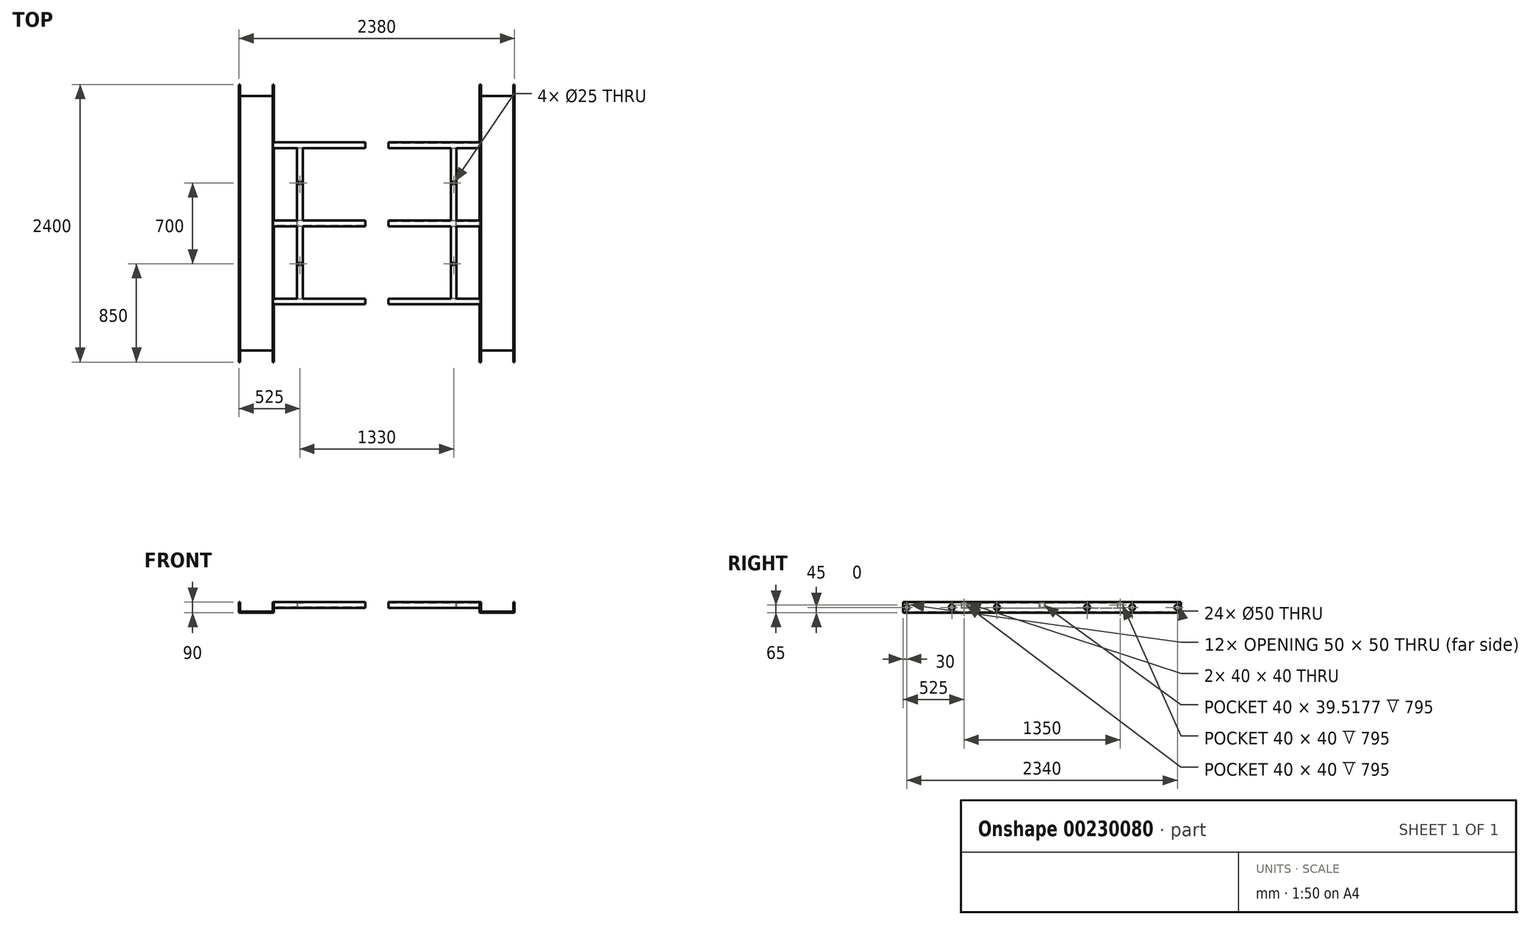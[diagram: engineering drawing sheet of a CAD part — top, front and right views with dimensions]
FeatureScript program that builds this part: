
annotation { "Feature Type Name" : "Feature", "Feature Type Description" : "" }
export const myFeature = defineFeature(function(context is Context, id is Id, definition is map)
    precondition{}
    {
        {
            var Q0;
            Q0=qCreatedBy(makeId("Front.planeOp"),FACE);
            var sketch = newSketch(context, id + "F0", { "sketchPlane" : qUnion([Q0])});
            skLineSegment(sketch, "E0", {"start": v(-890, 0) * mm, "end": v(-1190, 0) * mm});
            skLineSegment(sketch, "E1", {"start": v(-1190, 0) * mm, "end": v(-1190, 90) * mm});
            skLineSegment(sketch, "E2", {"start": v(-1190, 90) * mm, "end": v(-1180, 90) * mm});
            skLineSegment(sketch, "E3", {"start": v(-1180, 90) * mm, "end": v(-1180, 10) * mm});
            skLineSegment(sketch, "E4", {"start": v(-1180, 10) * mm, "end": v(-900, 10) * mm});
            skLineSegment(sketch, "E5", {"start": v(-900, 10) * mm, "end": v(-900, 90) * mm});
            skLineSegment(sketch, "E6", {"start": v(-900, 90) * mm, "end": v(-890, 90) * mm});
            skLineSegment(sketch, "E7", {"start": v(-890, 90) * mm, "end": v(-890, 0) * mm});
            skSolve(sketch);
        }
        {
            var Q0;
            Q0 = qSketchRegion(id + "F0", true);
            extrude(context, id + "F1", {"entities" : qUnion([Q0]), "endBound" : BoundingType.SYMMETRIC, "depth" : 2400 * mm});
        }
        {
            var Q0;
            Q0=makeQuery(id+"F1.opExtrude","SWEPT_FACE",FACE,{"disambiguationData":[OSD([sQuery(id+"F0.wireOp",EDGE,"E4")])]});
            var sketch = newSketch(context, id + "F2", { "sketchPlane" : qUnion([Q0])});
            skLineSegment(sketch, "E8.bottom", {"start": v(-1180, 1200) * mm, "end": v(-900, 1200) * mm});
            skLineSegment(sketch, "E8.top", {"start": v(-1180, 1100) * mm, "end": v(-900, 1100) * mm});
            skLineSegment(sketch, "E8.left", {"start": v(-1180, 1200) * mm, "end": v(-1180, 1100) * mm});
            skLineSegment(sketch, "E8.right", {"start": v(-900, 1200) * mm, "end": v(-900, 1100) * mm});
            skLineSegment(sketch, "E9.bottom", {"start": v(-1180, -1200) * mm, "end": v(-900, -1200) * mm});
            skLineSegment(sketch, "E9.top", {"start": v(-1180, -1100) * mm, "end": v(-900, -1100) * mm});
            skLineSegment(sketch, "E9.left", {"start": v(-1180, -1200) * mm, "end": v(-1180, -1100) * mm});
            skLineSegment(sketch, "E9.right", {"start": v(-900, -1200) * mm, "end": v(-900, -1100) * mm});
            skSolve(sketch);
        }
        {
            var Q0;
            Q0 = qSketchRegion(id + "F2", true);
            extrude(context, id + "F3", {"entities" : qUnion([Q0]), "operationType" : NewBodyOperationType.REMOVE, "oppositeDirection" : true, "depth" : 25 * mm});
        }
        {
            var Q0;
            Q0=makeQuery(id+"F1.opExtrude","SWEPT_FACE",FACE,{"disambiguationData":[OSD([sQuery(id+"F0.wireOp",EDGE,"E7")])]});
            var sketch = newSketch(context, id + "F4", { "sketchPlane" : qUnion([Q0])});
            skLineSegment(sketch, "E10.bottom", {"start": v(-700, 90) * mm, "end": v(-650, 90) * mm});
            skLineSegment(sketch, "E10.top", {"start": v(-700, 40) * mm, "end": v(-650, 40) * mm});
            skLineSegment(sketch, "E10.left", {"start": v(-700, 90) * mm, "end": v(-700, 40) * mm});
            skLineSegment(sketch, "E10.right", {"start": v(-650, 90) * mm, "end": v(-650, 40) * mm});
            skLineSegment(sketch, "E11.bottom", {"start": v(650, 90) * mm, "end": v(700, 90) * mm});
            skLineSegment(sketch, "E11.top", {"start": v(650, 40) * mm, "end": v(700, 40) * mm});
            skLineSegment(sketch, "E11.left", {"start": v(650, 90) * mm, "end": v(650, 40) * mm});
            skLineSegment(sketch, "E11.right", {"start": v(700, 90) * mm, "end": v(700, 40) * mm});
            skLineSegment(sketch, "E12.bottom", {"start": v(-25, 90) * mm, "end": v(25, 90) * mm});
            skLineSegment(sketch, "E12.top", {"start": v(-25, 40.48) * mm, "end": v(25, 40.48) * mm});
            skLineSegment(sketch, "E12.left", {"start": v(-25, 90) * mm, "end": v(-25, 40.48) * mm});
            skLineSegment(sketch, "E12.right", {"start": v(25, 90) * mm, "end": v(25, 40.48) * mm});
            skSolve(sketch);
        }
        {
            var Q0;
            Q0 = qSketchRegion(id + "F4", true);
            extrude(context, id + "F5", {"entities" : qUnion([Q0]), "operationType" : NewBodyOperationType.ADD, "depth" : 790 * mm});
        }
        {
            var Q0;
            Q0=makeQuery(id+"F5.opExtrude","SWEPT_FACE",FACE,{"disambiguationData":[OSD([sQuery(id+"F4.wireOp",EDGE,"E11.left")])]});
            var sketch = newSketch(context, id + "F6", { "sketchPlane" : qUnion([Q0])});
            skLineSegment(sketch, "E13.bottom", {"start": v(-690, 90) * mm, "end": v(-640, 90) * mm});
            skLineSegment(sketch, "E13.top", {"start": v(-690, 40) * mm, "end": v(-685, 40) * mm});
            skLineSegment(sketch, "E13.left", {"start": v(-690, 90) * mm, "end": v(-690, 40) * mm});
            skLineSegment(sketch, "E13.right", {"start": v(-640, 90) * mm, "end": v(-640, 85) * mm});
            skLineSegment(sketch, "E14", {"start": v(-640, 85) * mm, "end": v(-685, 85) * mm});
            skLineSegment(sketch, "E15", {"start": v(-685, 85) * mm, "end": v(-685, 40) * mm});
            skSolve(sketch);
        }
        {
            var Q0;
            Q0 = qSketchRegion(id + "F6", true);
            var Q1;
            Q1=makeQuery(id+"F5.opExtrude","SWEPT_FACE",FACE,{"disambiguationData":[OSD([sQuery(id+"F4.wireOp",EDGE,"E10.right")])]});
            extrude(context, id + "F7", {"entities" : qUnion([Q0]), "operationType" : NewBodyOperationType.ADD, "endBound" : BoundingType.UP_TO_SURFACE, "endBoundEntityFace" : qUnion([Q1]), "depth" : 25 * mm});
        }
        {
            var Q0;
            Q0=makeQuery(id+"F5.opExtrude","CAP_FACE",FACE,{"disambiguationData":[OSD([sQuery(id+"F4.wireOp",EDGE,"E10.bottom"),sQuery(id+"F4.wireOp",EDGE,"E10.top"),sQuery(id+"F4.wireOp",EDGE,"E10.left"),sQuery(id+"F4.wireOp",EDGE,"E10.right")])],"isStart":false});
            var Q1;
            Q1=makeQuery(id+"F5.opExtrude","CAP_FACE",FACE,{"disambiguationData":[OSD([sQuery(id+"F4.wireOp",EDGE,"E12.bottom"),sQuery(id+"F4.wireOp",EDGE,"E12.top"),sQuery(id+"F4.wireOp",EDGE,"E12.left"),sQuery(id+"F4.wireOp",EDGE,"E12.right")])],"isStart":false});
            var Q2;
            Q2=makeQuery(id+"F5.opExtrude","CAP_FACE",FACE,{"disambiguationData":[OSD([sQuery(id+"F4.wireOp",EDGE,"E11.bottom"),sQuery(id+"F4.wireOp",EDGE,"E11.top"),sQuery(id+"F4.wireOp",EDGE,"E11.left"),sQuery(id+"F4.wireOp",EDGE,"E11.right")])],"isStart":false});
            shell(context, id + "F8", {"entities" : qUnion([Q0, Q1, Q2]), "thickness" : 5 * mm});
        }
        {
            var Q0;
            Q0=makeQuery(id+"F7.boolean.opBoolean","MERGE",FACE,{"derivedFrom":[makeQuery(id+"F5.boolean.opBoolean","MERGE",FACE,{"derivedFrom":[makeQuery(id+"F1.opExtrude","SWEPT_FACE",FACE,{"disambiguationData":[OSD([sQuery(id+"F0.wireOp",EDGE,"E6")])]}),makeQuery(id+"F5.opExtrude","SWEPT_FACE",FACE,{"disambiguationData":[OSD([sQuery(id+"F4.wireOp",EDGE,"E10.bottom")])]}),makeQuery(id+"F5.opExtrude","SWEPT_FACE",FACE,{"disambiguationData":[OSD([sQuery(id+"F4.wireOp",EDGE,"E11.bottom")])]})]}),makeQuery(id+"F7.opExtrude","SWEPT_FACE",FACE,{"disambiguationData":[OSD([sQuery(id+"F6.wireOp",EDGE,"E13.bottom")])]})]});
            var sketch = newSketch(context, id + "F9", { "sketchPlane" : qUnion([Q0])});
            skCircle(sketch, "E16", {"center": v(-665, 350) * mm, "radius": 12.5 * mm});
            skCircle(sketch, "E17", {"center": v(-665, -350) * mm, "radius": 12.5 * mm});
            skSolve(sketch);
        }
        {
            var Q0;
            Q0 = qSketchRegion(id + "F9", true);
            extrude(context, id + "F10", {"entities" : qUnion([Q0]), "operationType" : NewBodyOperationType.REMOVE, "oppositeDirection" : true, "depth" : 25 * mm});
        }
        {
            var Q0;
            Q0=makeQuery(id+"F1.opExtrude","SWEPT_FACE",FACE,{"disambiguationData":[OSD([sQuery(id+"F0.wireOp",EDGE,"E1")])]});
            var sketch = newSketch(context, id + "F11", { "sketchPlane" : qUnion([Q0])});
            skCircle(sketch, "E18", {"center": v(-1170, 45) * mm, "radius": 25 * mm});
            skPoint(sketch, "E18.centerSnap0", {"position": v(-1200, 45) * mm});
            skCircle(sketch, "E19", {"center": v(-780, 45) * mm, "radius": 25 * mm});
            skCircle(sketch, "E20", {"center": v(780, 45) * mm, "radius": 25 * mm});
            skCircle(sketch, "E21", {"center": v(1170, 45) * mm, "radius": 25 * mm});
            skCircle(sketch, "E22", {"center": v(-390, 45) * mm, "radius": 25 * mm});
            skCircle(sketch, "E23", {"center": v(390, 45) * mm, "radius": 25 * mm});
            skSolve(sketch);
        }
        {
            var Q0;
            Q0 = qSketchRegion(id + "F11", true);
            var Q1;
            Q1=makeQuery(id+"F1.opExtrude","SWEPT_FACE",FACE,{"disambiguationData":[OSD([sQuery(id+"F0.wireOp",EDGE,"E7")])]});
            extrude(context, id + "F12", {"entities" : qUnion([Q0]), "operationType" : NewBodyOperationType.REMOVE, "endBound" : BoundingType.UP_TO_SURFACE, "oppositeDirection" : true, "endBoundEntityFace" : qUnion([Q1]), "depth" : 25 * mm});
        }
        {
            var Q0;
            Q0=makeQuery(id+"F1.opExtrude","SWEPT_BODY",BODY,{"disambiguationData":[OSD([sQuery(id+"F0.wireOp",EDGE,"E0"),sQuery(id+"F0.wireOp",EDGE,"E1"),sQuery(id+"F0.wireOp",EDGE,"E2"),sQuery(id+"F0.wireOp",EDGE,"E3"),sQuery(id+"F0.wireOp",EDGE,"E4"),sQuery(id+"F0.wireOp",EDGE,"E5"),sQuery(id+"F0.wireOp",EDGE,"E6"),sQuery(id+"F0.wireOp",EDGE,"E7")])]});
            var Q1;
            Q1=qCreatedBy(makeId("Right.planeOp"),FACE);
            mirror(context, id + "F13", {"entities" : qUnion([Q0]), "mirrorPlane" : qUnion([Q1])});
        }
    });
